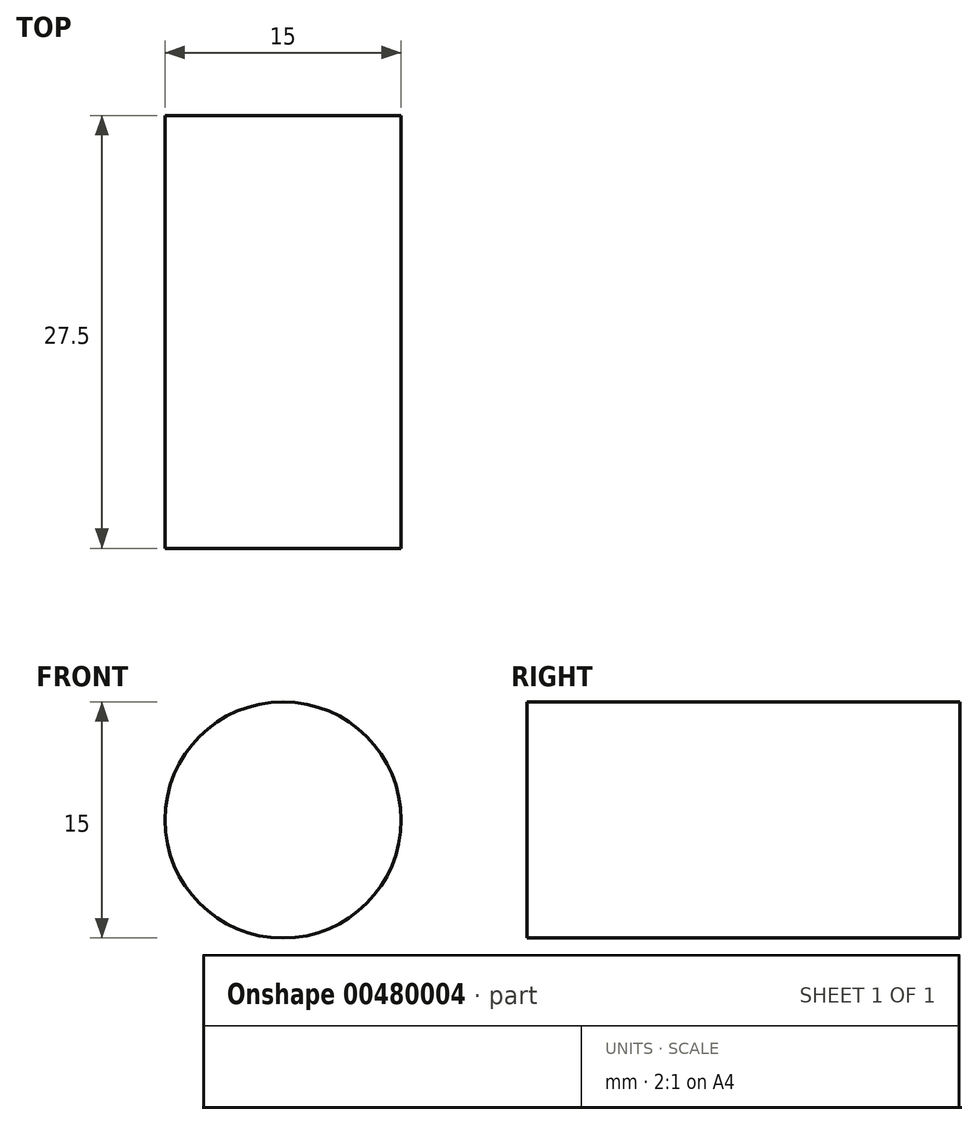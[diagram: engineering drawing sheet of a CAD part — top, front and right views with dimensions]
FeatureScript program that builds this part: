
annotation { "Feature Type Name" : "Feature", "Feature Type Description" : "" }
export const myFeature = defineFeature(function(context is Context, id is Id, definition is map)
    precondition{}
    {
        {
            var Q0;
            Q0=qCreatedBy(makeId("Front.planeOp"),FACE);
            var sketch = newSketch(context, id + "F0", { "sketchPlane" : qUnion([Q0])});
            skCircle(sketch, "E0", {"center": v(0, 0) * mm, "radius": 7.5 * mm});
            skSolve(sketch);
        }
        {
            var Q0;
            Q0=makeQuery(id+"F0.imprint","IMPRINT",FACE,{"disambiguationData":[TD([[makeQuery(id+"F0.imprint","IMPRINT",EDGE,{"derivedFrom":sQuery(id+"F0.wireOp",EDGE,"E0")}),1.0]])]});
            var Q1;
            Q1=sQuery(id+"F0.wireOp",EDGE,"E0");
            extrude(context, id + "F1", {"entities" : qUnion([Q0]), "surfaceEntities" : qUnion([Q1]), "depth" : 27.5 * mm});
        }
    });
